# Revit family: OASIS TS3P-6032 STD
name_source: partatom
category: Plumbing Fixtures
revit_build: Autodesk Revit 2013 (Build: 20130531_2115(x64)
units: mm (PartAtom-declared; Revit-internal decimal feet)

## types (5) — shared parameters
BIM Model By = www.epoch-design.com
Cold Water Connector = Cold Water Connection
Color = <By Category>
Grab Bar Finish = <By Category>
Hot Water Connector = Hot Water Connection
Manufacturer = OASIS
Sanitary Connector = Sanitary Connection
Seat Finish = <By Category>
Stainless steel = <By Category>
Type Comments = TUB/SHOWER
URL = www.oasisbath.com
Waste Connection = No

## per-type parameters (varying)
| type | Bar_Horz_Back_High | Bar_Horz_Back_Low | Bar_Horz_Left | Bar_Horz_Right_20" | Bar_Vert | Model |
| Base model, 3SF, 3SM, & FH packages | No | No | No | No | No | TS3P-6032 STD/(3SF,3SM,FH) |
| BP1-60 package | Yes | No | No | Yes | No | TS3P-6032 STD/BP1-60 |
| BP2-60 package | Yes | No | No | Yes | Yes | TS3P-6032 STD/BP2-60 |
| 4BAR package | Yes | Yes | Yes | Yes | No | TS3P-6032 STD/4BAR |
| 5BAR package | Yes | Yes | Yes | Yes | Yes | TS3P-6032 STD/5BAR |

## geometry (parser evidence)
native form markers: Sweep x10
no freeform markers — native parametric forms only
